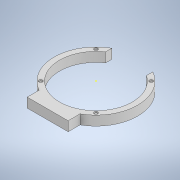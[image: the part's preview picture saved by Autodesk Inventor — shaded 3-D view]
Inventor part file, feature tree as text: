
AUTODESK INVENTOR PART (.ipt)
format: ipt  version: 2020 (Build 240168000, 168)  size: 158,720 bytes
history: native  units: mm
features: sketch x10, extrude x8
ambient origin geometry x8: Origin, YZ Plane, XZ Plane, XY Plane, X Axis, Y Axis, Z Axis, Center Point
bodies: Solid1 (feature_tree)
feature tree (18):
  extrude  "Extrusion1"  Depth=8.0mm TaperAngle=0.0deg
  extrude  "Extrusion2"  Depth=8.0mm TaperAngle=0.0deg
  extrude  "Extrusion3"  Depth=10.0mm
  extrude  "Extrusion4"  Depth=8.0mm TaperAngle=0.0deg
  sketch  "Sketch5"  dims[d12=32.75mm d13=135.0deg]
  extrude  "Extrusion5"  TaperAngle=135.0deg  [1 undecoded]
  extrude  "Extrusion6"  Depth=1.0mm TaperAngle=0.0deg
  extrude  "Extrusion7"  TaperAngle=135.0deg  [1 undecoded]
  extrude  "Extrusion8"  Depth=1.0mm TaperAngle=0.0deg
  sketch  "Sketch10"  dims[d23=45.0deg d24=3.0mm d25=1.0mm d26=0.0mm d27=32.75mm d28=45.0deg d29=3.0mm d30=1.0mm d31=0.0mm]
  sketch  "Sketch1"  dims[d0=70.0mm d1=8.0mm d2=0.0mm]
  sketch  "Sketch2"  dims[d3=61.0mm d4=8.0mm d5=0.0mm]
  sketch  "Sketch3"  dims[d6=34.336mm d7=10.0mm]
  sketch  "Sketch4"  dims[d8=8.0mm d9=0.0mm d10=8.0mm d11=0.0mm]
  sketch  "Sketch6"  dims[d14=3.0mm d15=1.0mm d16=0.0mm]
  sketch  "Sketch7"  dims[d17=32.75mm d18=135.0deg]
  sketch  "Sketch8"  dims[d19=3.0mm d20=1.0mm d21=0.0mm]
  sketch  "Sketch9"  dims[d22=32.75mm]
note: 2 required parameter values undecoded (feature->parameter linkage not recoverable at this tier; creation-order binding heuristic only, values carry confidence <= 0.55)
